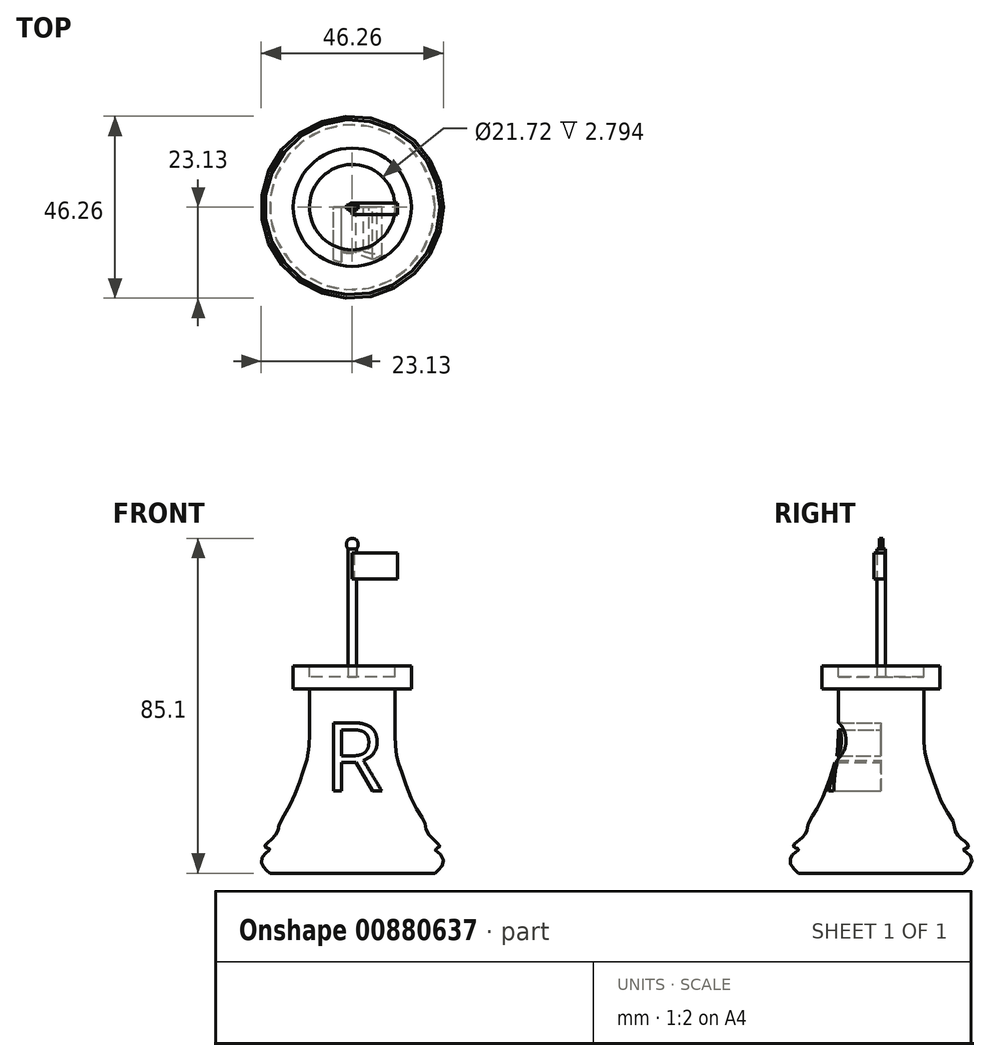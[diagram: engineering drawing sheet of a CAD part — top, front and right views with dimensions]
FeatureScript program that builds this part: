
annotation { "Feature Type Name" : "Feature", "Feature Type Description" : "" }
export const myFeature = defineFeature(function(context is Context, id is Id, definition is map)
    precondition{}
    {
        {
            var Q0;
            Q0=qCreatedBy(makeId("Front.planeOp"),FACE);
            var sketch = newSketch(context, id + "F0", { "sketchPlane" : qUnion([Q0])});
            skLineSegment(sketch, "E0", {"start": v(0, 52.03) * mm, "end": v(0, -48.54) * mm});
            skLineSegment(sketch, "E1", {"start": v(0, -48.54) * mm, "end": v(0, -38.41) * mm});
            skLineSegment(sketch, "E2", {"start": v(0, -38.41) * mm, "end": v(20.95, -38.41) * mm});
            skFitSpline(sketch, "E3", {"points": [v(20.95, -38.41) * mm, v(22.12, -37.3) * mm, v(23.07, -35.9) * mm, v(22.48, -33.7) * mm, v(20.95, -32.38) * mm, v(21.43, -32.05) * mm, v(22.26, -31.58) * mm, v(21.53, -30.6) * mm, v(20.4, -29.66) * mm, v(18.83, -27.59) * mm, v(18.47, -25.61) * mm, v(16.03, -21.57) * mm, v(12.34, -12.2) * mm, v(11.1, -7.64) * mm, v(10.86, -1.96) * mm, v(10.86, 0) * mm], "startDerivative": vector(21.79, 20.55) * mm, "endDerivative": vector(0.03, 27.98) * mm});
            skLineSegment(sketch, "E4", {"start": v(10.86, 0) * mm, "end": v(10.86, 8.38) * mm});
            skPoint(sketch, "E5.1.internal.orphan", {"position": v(15.02, 8.38) * mm});
            skLineSegment(sketch, "E6", {"start": v(10.86, 8.38) * mm, "end": v(15.02, 8.38) * mm});
            skLineSegment(sketch, "E7", {"start": v(15.02, 8.38) * mm, "end": v(15.02, 14.32) * mm});
            skLineSegment(sketch, "E8", {"start": v(15.02, 14.32) * mm, "end": v(10.86, 14.32) * mm});
            skLineSegment(sketch, "E9", {"start": v(10.86, 14.32) * mm, "end": v(10.86, 11.52) * mm});
            skLineSegment(sketch, "E10", {"start": v(10.86, 11.52) * mm, "end": v(0, 11.52) * mm});
            skSolve(sketch);
        }
        {
            var Q0;
            {var subQ0=sQuery(id+"F0.wireOp",EDGE,"E2");Q0=makeQuery(id+"F0.imprint","IMPRINT",FACE,{"disambiguationData":[TD([[makeQuery(id+"F0.imprint","IMPRINT",EDGE,{"derivedFrom":subQ0}),1.0]])]});}
            var Q1;
            Q1=sQuery(id+"F0.wireOp",EDGE,"E0");
            revolve(context, id + "F1", {"surfaceOperationType" : NewSurfaceOperationType.NEW, "entities" : qUnion([Q0]), "axis" : qUnion([Q1]), "revolveType" : RevolveType.FULL});
        }
        {
            var Q0;
            Q0=qCreatedBy(makeId("Front.planeOp"),FACE);
            var sketch = newSketch(context, id + "F2", { "sketchPlane" : qUnion([Q0])});
            skText(sketch, "E11", { "text": "R", "fontName": "OpenSans-Regular.ttf"});
            const initialGuessF2  = {"E11": [-0.0071, -0.0175, 1, 0, 0.0175]};
            skSetInitialGuess(sketch, initialGuessF2);
            skSolve(sketch);
        }
        {
            var Q0;
            Q0 = qSketchRegion(id + "F2", true);
            extrude(context, id + "F3", {"entities" : qUnion([Q0]), "operationType" : NewBodyOperationType.REMOVE, "depth" : 49 * mm, "offsetDistance" : 25 * mm});
        }
        {
            var Q0;
            Q0=qCreatedBy(makeId("Top.planeOp"),FACE);
            var sketch = newSketch(context, id + "F4", { "sketchPlane" : qUnion([Q0])});
            skCircle(sketch, "E12", {"center": v(0, 0) * mm, "radius": 1.1 * mm});
            skSolve(sketch);
        }
        {
            var Q0;
            Q0 = qSketchRegion(id + "F4", true);
            extrude(context, id + "F5", {"entities" : qUnion([Q0]), "operationType" : NewBodyOperationType.ADD, "depth" : 44 * mm, "offsetDistance" : 25 * mm});
        }
        {
            var Q0;
            Q0=qCreatedBy(makeId("Front.planeOp"),FACE);
            var sketch = newSketch(context, id + "F6", { "sketchPlane" : qUnion([Q0])});
            skPoint(sketch, "E13.0.internal.orphan", {"position": v(0, 42.97) * mm});
            skPoint(sketch, "E14.endDerivative.orphan", {"position": v(11.5, 36.4) * mm});
            skPoint(sketch, "E15.6.internal.orphan", {"position": v(0, 36.4) * mm});
            skLineSegment(sketch, "E16", {"start": v(0, 36.4) * mm, "end": v(11.5, 36.4) * mm});
            skLineSegment(sketch, "E17", {"start": v(0, 42.97) * mm, "end": v(11.5, 42.97) * mm});
            skLineSegment(sketch, "E18", {"start": v(11.5, 42.97) * mm, "end": v(11.5, 36.4) * mm});
            skLineSegment(sketch, "E19", {"start": v(0, 42.97) * mm, "end": v(0, 36.4) * mm});
            skCircle(sketch, "E20", {"center": v(0, 44.7) * mm, "radius": 0.75 * mm});
            skSolve(sketch);
        }
        {
            var Q0;
            Q0=makeQuery(id+"F6.imprint","IMPRINT",FACE,{"disambiguationData":[TD([[makeQuery(id+"F6.imprint","IMPRINT",EDGE,{"derivedFrom":sQuery(id+"F6.wireOp",EDGE,"E16")}),1.0]])]});
            extrude(context, id + "F7", {"entities" : qUnion([Q0]), "operationType" : NewBodyOperationType.ADD, "depth" : 1.8 * mm, "offsetDistance" : 25 * mm, "hasSecondDirection" : true, "secondDirectionOppositeDirection" : true, "secondDirectionDepth" : 1 * mm});
        }
        {
            var Q0;
            Q0=qCreatedBy(makeId("Front.planeOp"),FACE);
            var sketch = newSketch(context, id + "F8", { "sketchPlane" : qUnion([Q0])});
            skCircle(sketch, "E21", {"center": v(0, 45.18) * mm, "radius": 1.52 * mm});
            skSolve(sketch);
        }
        {
            var Q0;
            Q0 = qSketchRegion(id + "F8", true);
            extrude(context, id + "F9", {"entities" : qUnion([Q0]), "operationType" : NewBodyOperationType.ADD, "depth" : 0.46 * mm, "offsetDistance" : 25 * mm, "hasSecondDirection" : true, "secondDirectionOppositeDirection" : true, "secondDirectionDepth" : 0.51 * mm});
        }
    });
